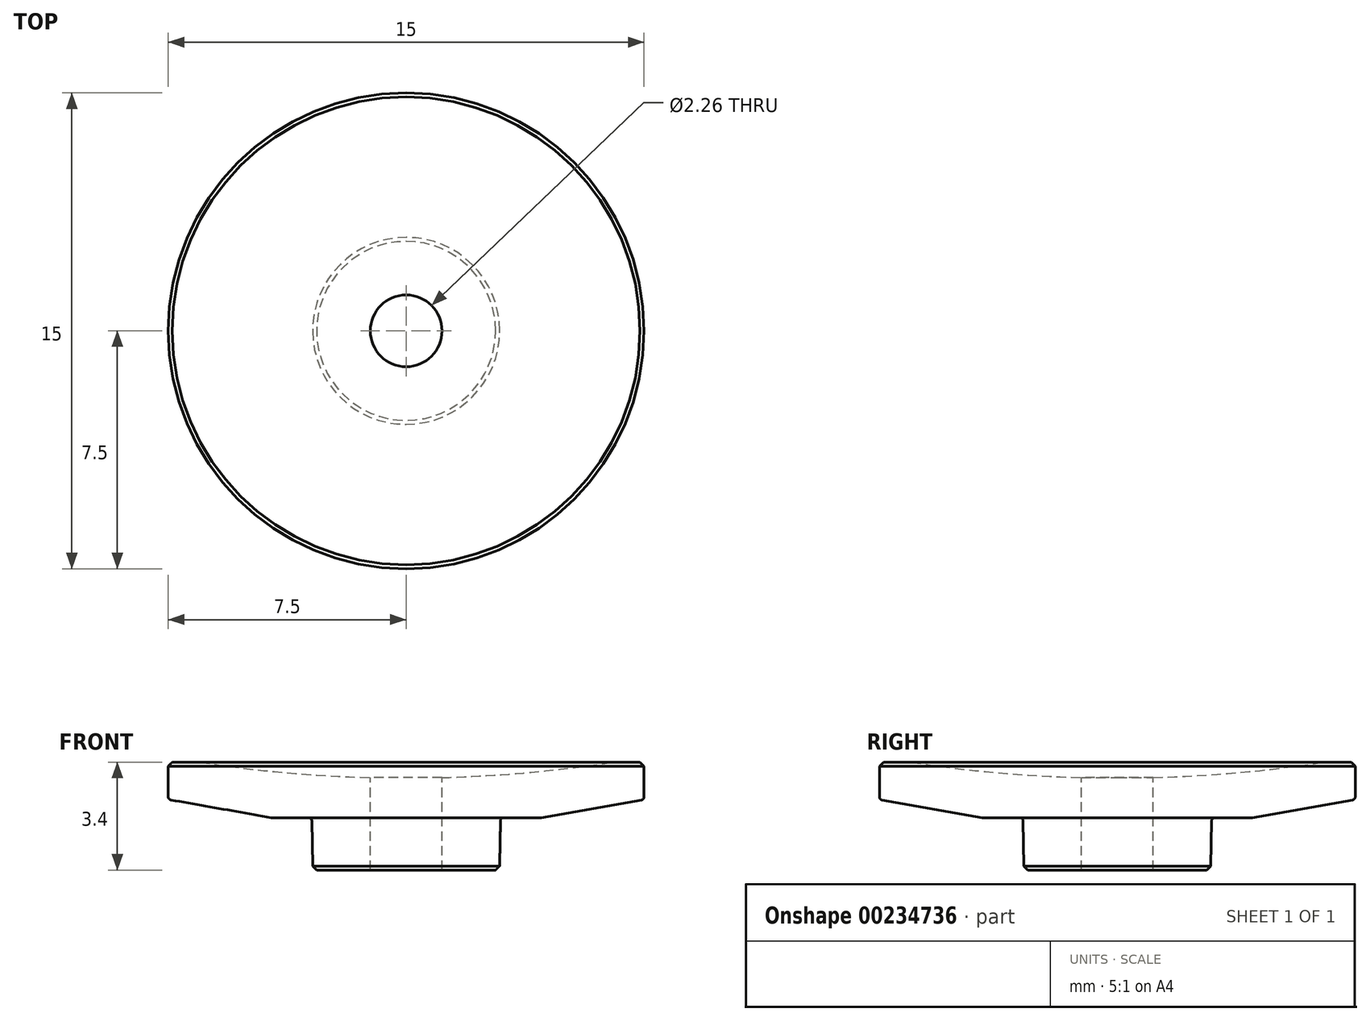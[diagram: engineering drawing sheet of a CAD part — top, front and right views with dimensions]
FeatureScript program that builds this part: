
annotation { "Feature Type Name" : "Feature", "Feature Type Description" : "" }
export const myFeature = defineFeature(function(context is Context, id is Id, definition is map)
    precondition{}
    {
        {
            var Q0;
            Q0=qCreatedBy(makeId("Front.planeOp"),FACE);
            var sketch = newSketch(context, id + "F0", { "sketchPlane" : qUnion([Q0])});
            skLineSegment(sketch, "E0", {"start": v(0, 0) * mm, "end": v(2.95, 0) * mm});
            skLineSegment(sketch, "E1", {"start": v(2.95, 0) * mm, "end": v(2.97, 1.65) * mm});
            skLineSegment(sketch, "E2", {"start": v(2.97, 1.65) * mm, "end": v(4.24, 1.65) * mm});
            skLineSegment(sketch, "E3", {"start": v(4.24, 1.65) * mm, "end": v(7.5, 2.22) * mm});
            skLineSegment(sketch, "E4", {"start": v(7.5, 2.22) * mm, "end": v(7.5, 3.4) * mm});
            skLineSegment(sketch, "E5", {"start": v(7.5, 3.4) * mm, "end": v(6.5, 3.4) * mm});
            skLineSegment(sketch, "E6", {"start": v(0, 2.9) * mm, "end": v(0, 0) * mm});
            skArc(sketch, "E7", {"start": v(0, 2.9) * mm, "mid": v(3.26, 3.03) * mm, "end": v(6.5, 3.4) * mm});
            skPoint(sketch, "E8.orphan", {"position": v(0, 3.4) * mm});
            skLineSegment(sketch, "E9", {"start": v(0, 0) * mm, "end": v(0, -2.37) * mm, "construction": true});
            skSolve(sketch);
        }
        {
            var Q0;
            Q0=qSketchRegion(id+"F0",true);
            var Q1;
            Q1=sQuery(id+"F0.wireOp",EDGE,"E6");
            revolve(context, id + "F1", {"entities" : qUnion([Q0]), "axis" : qUnion([Q1]), "revolveType" : RevolveType.FULL});
        }
        {
            var Q0;
            Q0=makeQuery(id+"F1.opRevolve","SWEPT_EDGE",EDGE,{"disambiguationData":[OSD([sQuery(id+"F0.wireOp",EDGE,"E0"),sQuery(id+"F0.wireOp",EDGE,"E1")])]});
            var Q1;
            Q1=makeQuery(id+"F1.opRevolve","SWEPT_EDGE",EDGE,{"disambiguationData":[OSD([sQuery(id+"F0.wireOp",EDGE,"E4"),sQuery(id+"F0.wireOp",EDGE,"E5")])]});
            chamfer(context, id + "F2", {"entities" : qUnion([Q0, Q1]), "width" : 0.13 * mm, "tangentPropagation" : true});
        }
        {
            var Q0;
            Q0=makeQuery(id+"F1.opRevolve","SWEPT_EDGE",EDGE,{"disambiguationData":[OSD([sQuery(id+"F0.wireOp",EDGE,"KmEllf09-JBKP-2wvp-Ln3d-dT31Av5gxA5O"),sQuery(id+"F0.wireOp",EDGE,"SqjkA4CO-rQVQ-ybkh-YT7C-LuhsKEooFiCv")])]});
            var Q1;
            Q1=makeQuery(id+"F1.opRevolve","SWEPT_EDGE",EDGE,{"disambiguationData":[OSD([sQuery(id+"F0.wireOp",EDGE,"E3"),sQuery(id+"F0.wireOp",EDGE,"KmEllf09-JBKP-2wvp-Ln3d-dT31Av5gxA5O")])]});
            var Q2;
            Q2=makeQuery(id+"F1.opRevolve","SWEPT_EDGE",EDGE,{"disambiguationData":[OSD([sQuery(id+"F0.wireOp",EDGE,"E2"),sQuery(id+"F0.wireOp",EDGE,"E3")])]});
            var Q3;
            Q3=makeQuery(id+"F1.opRevolve","SWEPT_EDGE",EDGE,{"disambiguationData":[OSD([sQuery(id+"F0.wireOp",EDGE,"E5"),sQuery(id+"F0.wireOp",EDGE,"E7")])]});
            var Q4;
            Q4=makeQuery(id+"F1.opRevolve","SWEPT_EDGE",EDGE,{"disambiguationData":[OSD([sQuery(id+"F0.wireOp",EDGE,"E1"),sQuery(id+"F0.wireOp",EDGE,"E2")])]});
            fillet(context, id + "F3", {"entities" : qUnion([Q0, Q1, Q2, Q3, Q4]), "radius" : .1 * mm, "tangentPropagation" : true, "allowEdgeOverflow" : false});
        }
        {
            var Q0;
            Q0=makeQuery(id+"F1.opRevolve","SWEPT_FACE",FACE,{"disambiguationData":[OSD([sQuery(id+"F0.wireOp",EDGE,"E5")])]});
            var sketch = newSketch(context, id + "F4", { "sketchPlane" : qUnion([Q0])});
            skPoint(sketch, "E10.0", {"position": v(0, 0) * mm});
            skSolve(sketch);
        }
        {
            var Q0;
            Q0=sQuery(id+"F4.wireOp",VERTEX,"E10.0");
            var Q1;
            Q1=makeQuery(id+"F1.opRevolve","SWEPT_BODY",BODY,{"disambiguationData":[OSD([sQuery(id+"F0.wireOp",EDGE,"E0"),sQuery(id+"F0.wireOp",EDGE,"E1"),sQuery(id+"F0.wireOp",EDGE,"E2"),sQuery(id+"F0.wireOp",EDGE,"E3"),sQuery(id+"F0.wireOp",EDGE,"E4"),sQuery(id+"F0.wireOp",EDGE,"E5"),sQuery(id+"F0.wireOp",EDGE,"E6"),sQuery(id+"F0.wireOp",EDGE,"E7")])]});
            hole(context, id + "F5", {"style" : HoleStyle.SIMPLE, "endStyle" : HoleEndStyle.BLIND, "standardTappedOrClearance" : lookupTablePath({ "standard" : "ANSI", "engagement" : "75%", "pitch" : "40 tpi", "size" : "#4", "type" : "Tapped" }), "standardBlindInLast" : lookupTablePath({ "standard" : "ANSI", "engagement" : "75%", "pitch" : "40 tpi", "size" : "#4", "type" : "Tapped" }), "holeDiameter" : 2.26 * mm, "holeDepth" : 12.7 * mm, "startFromSketch" : true, "locations" : qUnion([Q0]), "scope" : qUnion([Q1]), "majorDiameter" : 2.84 * mm});
        }
    });
